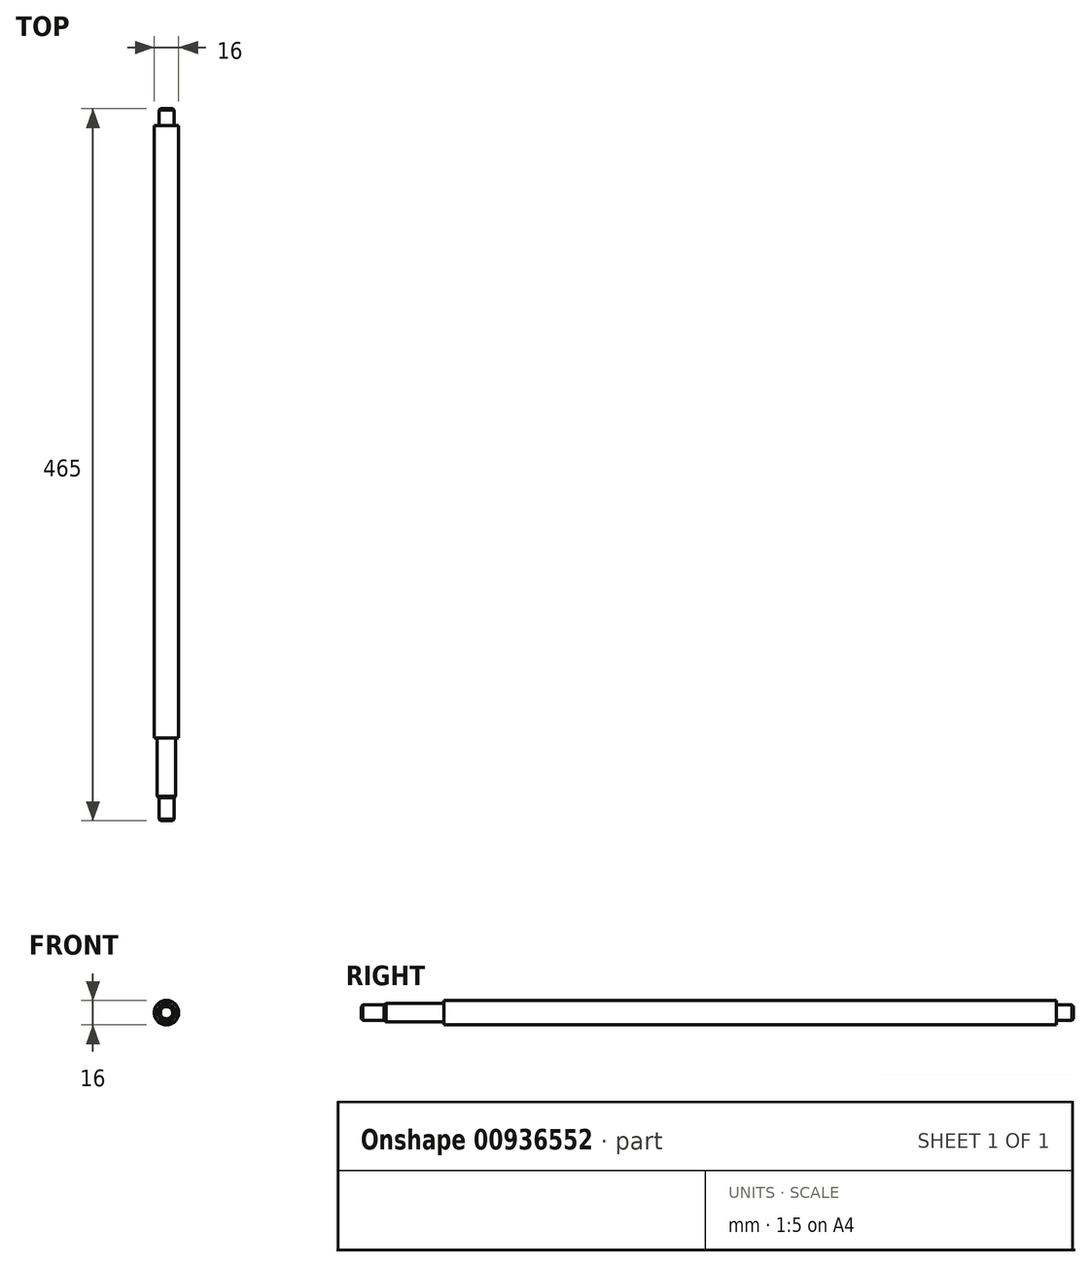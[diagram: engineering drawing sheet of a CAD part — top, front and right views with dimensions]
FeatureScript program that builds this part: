
annotation { "Feature Type Name" : "Feature", "Feature Type Description" : "" }
export const myFeature = defineFeature(function(context is Context, id is Id, definition is map)
    precondition{}
    {
        {
            var Q0;
            Q0=qCreatedBy(makeId("Right.planeOp"),FACE);
            var sketch = newSketch(context, id + "F0", { "sketchPlane" : qUnion([Q0])});
            skLineSegment(sketch, "E0", {"start": v(0, 0) * mm, "end": v(0, 5) * mm});
            skLineSegment(sketch, "E1", {"start": v(0, 5) * mm, "end": v(15, 5) * mm});
            skLineSegment(sketch, "E2", {"start": v(15, 5) * mm, "end": v(15, 6) * mm});
            skLineSegment(sketch, "E3", {"start": v(15, 6) * mm, "end": v(54, 6) * mm});
            skLineSegment(sketch, "E4", {"start": v(54, 8) * mm, "end": v(54, 6) * mm});
            skLineSegment(sketch, "E5", {"start": v(54, 8) * mm, "end": v(454, 8) * mm});
            skLineSegment(sketch, "E6", {"start": v(-5.84, 0) * mm, "end": v(694.16, 0) * mm, "construction": true});
            skLineSegment(sketch, "E7", {"start": v(454, 8) * mm, "end": v(454, 5) * mm});
            skLineSegment(sketch, "E8", {"start": v(454, 5) * mm, "end": v(465, 5) * mm});
            skLineSegment(sketch, "E9", {"start": v(465, 5) * mm, "end": v(465, 0) * mm});
            skLineSegment(sketch, "E10", {"start": v(465, 0) * mm, "end": v(0, 0) * mm});
            skSolve(sketch);
        }
        {
            var Q0;
            Q0=qSketchRegion(id+"F0",true);
            var Q1;
            Q1=sQuery(id+"F0.wireOp",EDGE,"E6");
            revolve(context, id + "F1", {"surfaceOperationType" : NewSurfaceOperationType.NEW, "entities" : qUnion([Q0]), "axis" : qUnion([Q1]), "revolveType" : RevolveType.FULL});
        }
        {
            var Q0;
            Q0=makeQuery(id+"F1.opRevolve","SWEPT_EDGE",EDGE,{"disambiguationData":[OSD([sQuery(id+"F0.wireOp",EDGE,"E0"),sQuery(id+"F0.wireOp",EDGE,"E1")])]});
            var Q1;
            Q1=makeQuery(id+"F1.opRevolve","SWEPT_EDGE",EDGE,{"disambiguationData":[OSD([sQuery(id+"F0.wireOp",EDGE,"E2"),sQuery(id+"F0.wireOp",EDGE,"E3")])]});
            var Q2;
            Q2=makeQuery(id+"F1.opRevolve","SWEPT_EDGE",EDGE,{"disambiguationData":[OSD([sQuery(id+"F0.wireOp",EDGE,"E8"),sQuery(id+"F0.wireOp",EDGE,"E9")])]});
            chamfer(context, id + "F2", {"entities" : qUnion([Q0, Q1, Q2]), "width" : 1 * mm, "tangentPropagation" : true});
        }
    });
